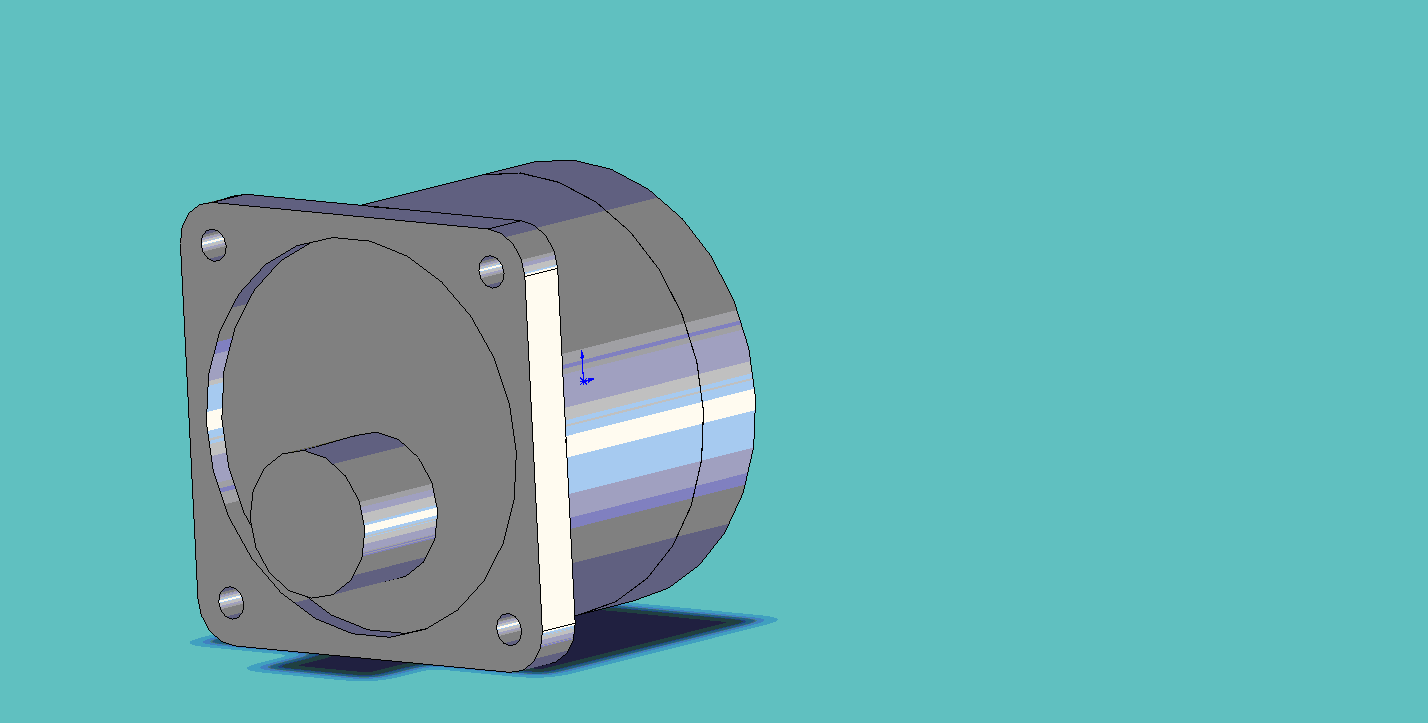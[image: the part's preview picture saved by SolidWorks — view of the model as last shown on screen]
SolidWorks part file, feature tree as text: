
SOLIDWORKS PART (.sldprt)
format: sldprt  version: not decoded by parser v0  size: 171,520 bytes
history: native  units: mm
features: sketch x5, plane x3, cut_extrude x2, material x1, revolve x1, extrude x1, fillet x1, cut_revolve x1 (+8 scaffold rows collapsed)
feature tree (23):
  scaffold x8  (default folders/planes/origin — collapsed)
  material  "Matériau <non spécifié>"
  plane  "Plan de face"
  plane  "Plan de dessus"
  plane  "Plan de droite"
  sketch  "Esquisse1"  dims[D1=30.0mm D2=29.98mm D3=5.4mm D4=19.6mm]
  revolve  "Révolution1"  Angle=360deg
  sketch  "Esquisse2"  dims[c1.D6=2.2mm c1.D2=30.0mm c1.D3=15.0mm c1.D4=15.0mm c1.D1=24.2mm c1.D5=30.0mm c2.D1=3.0mm]
  extrude  "Extrusion1"  Depth=3.4mm
  sketch  "Esquisse3"  dims[D1=27.0mm]
  cut_extrude  "Enlèv. mat.-Extru.1"  Depth=1.6mm
  fillet  "Congé1"  Radius=3mm
  sketch  "Esquisse4"  dims[D2=10.0mm D1=4.9mm]
  cut_extrude  "Extrusion2"  Depth=7.55mm
  sketch  "Esquisse5"  dims[D1=3.0mm D2=1.1mm D3=8.5mm D4=2.0mm D5=4.2mm D6=8.0mm]
  cut_revolve  "Enlèvement de matière-Révolution1"  Angle=360deg
decode coverage: 11 of 11 modeling features carry decoded parameters
note: suppression state not decoded; provenance and decode notes live in map.json
